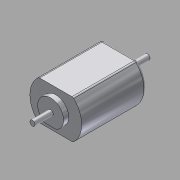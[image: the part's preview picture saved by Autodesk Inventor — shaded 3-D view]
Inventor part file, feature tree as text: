
AUTODESK INVENTOR PART (.ipt)
format: ipt  version: 2015 (Build 190159000, 159)  size: 138,752 bytes
history: native  units: in
note: dims shown in document units (in); Inventor stores cm internally (conversion verified against a paired STEP export)
features: sketch x5, other x3
ambient origin geometry x8: Origin, YZ Plane, XZ Plane, XY Plane, X Axis, Y Axis, Z Axis, Center Point
bodies: Solid1 (feature_tree)
feature tree (8):
  other  "motor_MIR2.ipt"
  other  "Solid1::motor_MIR2.ipt"
  other  "TaggingFeature1"
  sketch  "Sketch1"  dims[d0=0.3937in]
  sketch  "Sketch2"
  sketch  "Sketch3"
  sketch  "Sketch4"
  sketch  "Sketch5"
